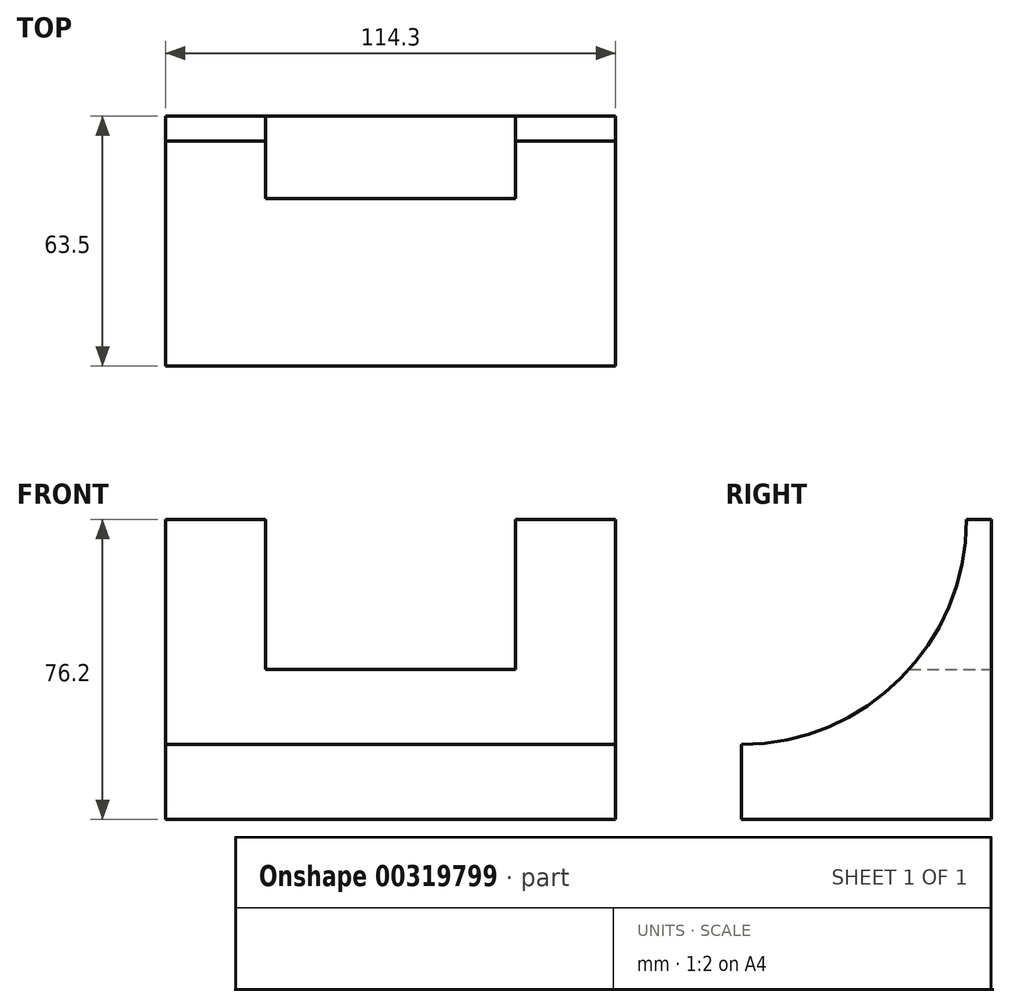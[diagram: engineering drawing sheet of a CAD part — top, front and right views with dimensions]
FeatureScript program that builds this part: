
annotation { "Feature Type Name" : "Feature", "Feature Type Description" : "" }
export const myFeature = defineFeature(function(context is Context, id is Id, definition is map)
    precondition{}
    {
        {
            var Q0;
            Q0=qCreatedBy(makeId("Front.planeOp"),FACE);
            var sketch = newSketch(context, id + "F0", { "sketchPlane" : qUnion([Q0])});
            skLineSegment(sketch, "E0.bottom", {"start": v(-49, 35.2) * mm, "end": v(65.3, 35.2) * mm});
            skLineSegment(sketch, "E0.top", {"start": v(-49, -41) * mm, "end": v(65.3, -41) * mm});
            skLineSegment(sketch, "E0.left", {"start": v(-49, 35.2) * mm, "end": v(-49, -41) * mm});
            skLineSegment(sketch, "E0.right", {"start": v(65.3, 35.2) * mm, "end": v(65.3, -41) * mm});
            skSolve(sketch);
        }
        {
            var Q0;
            Q0=makeQuery(id+"F0.imprint","IMPRINT",FACE,{"disambiguationData":[TD([[makeQuery(id+"F0.imprint","IMPRINT",EDGE,{"derivedFrom":sQuery(id+"F0.wireOp",EDGE,"E0.bottom")}),-1.0]])]});
            extrude(context, id + "F1", {"entities" : qUnion([Q0]), "oppositeDirection" : true, "depth" : 63.5 * mm});
        }
        {
            var Q0;
            Q0=makeQuery(id+"F1.opExtrude","SWEPT_FACE",FACE,{"disambiguationData":[OSD([sQuery(id+"F0.wireOp",EDGE,"E0.right")])]});
            var sketch = newSketch(context, id + "F2", { "sketchPlane" : qUnion([Q0])});
            skArc(sketch, "E1", {"start": v(0, -21.94) * mm, "mid": v(40.41, -5.2) * mm, "end": v(57.15, 35.2) * mm});
            skLineSegment(sketch, "E2", {"start": v(0, 35.2) * mm, "end": v(0, -21.94) * mm});
            skLineSegment(sketch, "E3", {"start": v(57.15, 35.2) * mm, "end": v(0, 35.2) * mm});
            skSolve(sketch);
        }
        {
            var Q0;
            Q0=makeQuery(id+"F2.imprint","IMPRINT",FACE,{"disambiguationData":[TD([[makeQuery(id+"F2.imprint","IMPRINT",EDGE,{"derivedFrom":sQuery(id+"F2.wireOp",EDGE,"E1")}),1.0]])]});
            extrude(context, id + "F3", {"entities" : qUnion([Q0]), "operationType" : NewBodyOperationType.REMOVE, "endBound" : BoundingType.THROUGH_ALL, "oppositeDirection" : true, "depth" : 25.4 * mm});
        }
        {
            var Q0;
            Q0=makeQuery(id+"F1.opExtrude","CAP_FACE",FACE,{"disambiguationData":[OSD([sQuery(id+"F0.wireOp",EDGE,"E0.bottom"),sQuery(id+"F0.wireOp",EDGE,"E0.top"),sQuery(id+"F0.wireOp",EDGE,"E0.left"),sQuery(id+"F0.wireOp",EDGE,"E0.right")])],"isStart":false});
            var sketch = newSketch(context, id + "F4", { "sketchPlane" : qUnion([Q0])});
            skLineSegment(sketch, "E4", {"start": v(-65.3, 35.2) * mm, "end": v(-39.9, 35.2) * mm});
            skLineSegment(sketch, "E5", {"start": v(49, 35.2) * mm, "end": v(23.6, 35.2) * mm});
            skLineSegment(sketch, "E6", {"start": v(23.6, 35.2) * mm, "end": v(23.6, -2.9) * mm});
            skLineSegment(sketch, "E7", {"start": v(23.6, -2.9) * mm, "end": v(-39.9, -2.9) * mm});
            skLineSegment(sketch, "E8", {"start": v(-39.9, -2.9) * mm, "end": v(-39.9, 35.2) * mm});
            skSolve(sketch);
        }
        {
            var Q0;
            {var subQ0=sQuery(id+"F4.wireOp",EDGE,"E6");Q0=makeQuery(id+"F4.imprint","IMPRINT",FACE,{"disambiguationData":[TD([[makeQuery(id+"F4.imprint","IMPRINT",EDGE,{"derivedFrom":subQ0}),-1.0]])]});}
            extrude(context, id + "F5", {"entities" : qUnion([Q0]), "operationType" : NewBodyOperationType.REMOVE, "endBound" : BoundingType.THROUGH_ALL, "oppositeDirection" : true, "depth" : 25.4 * mm});
        }
    });
